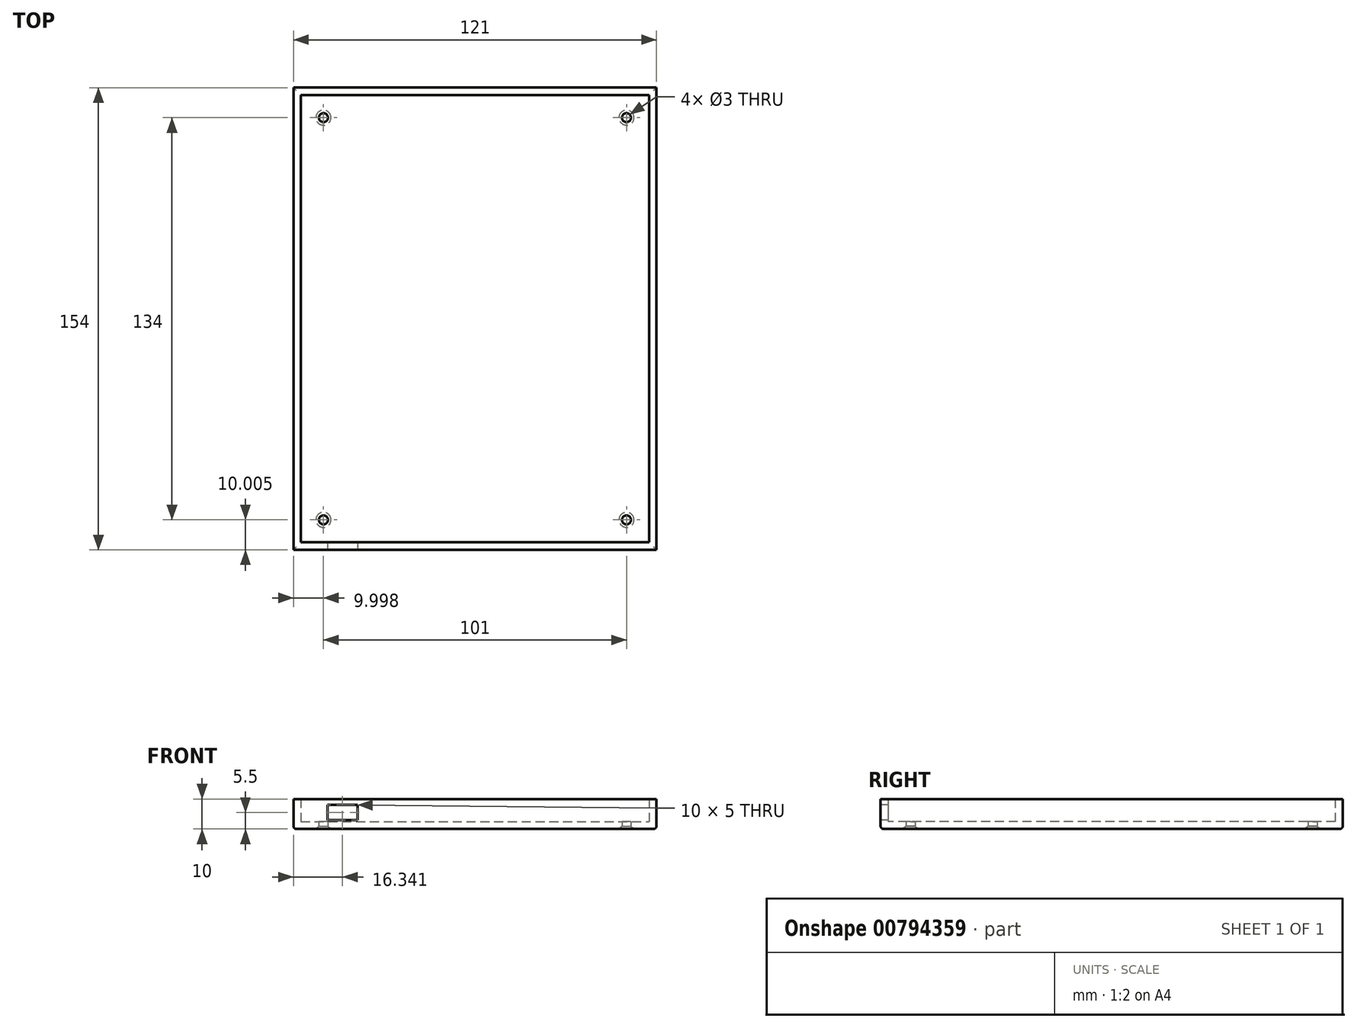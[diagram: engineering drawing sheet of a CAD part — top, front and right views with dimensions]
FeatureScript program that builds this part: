
annotation { "Feature Type Name" : "Feature", "Feature Type Description" : "" }
export const myFeature = defineFeature(function(context is Context, id is Id, definition is map)
    precondition{}
    {
        {
            var Q0;
            Q0=qCreatedBy(makeId("Top.planeOp"),FACE);
            var sketch = newSketch(context, id + "F0", { "sketchPlane" : qUnion([Q0])});
            skLineSegment(sketch, "E0.bottom", {"start": v(-90.74, 109.84) * mm, "end": v(30.26, 109.84) * mm});
            skLineSegment(sketch, "E0.top", {"start": v(-90.74, -44.16) * mm, "end": v(30.26, -44.16) * mm});
            skLineSegment(sketch, "E0.left", {"start": v(-90.74, 109.84) * mm, "end": v(-90.74, -44.16) * mm});
            skLineSegment(sketch, "E0.right", {"start": v(30.26, 109.84) * mm, "end": v(30.26, -44.16) * mm});
            skSolve(sketch);
        }
        {
            var Q0;
            Q0=makeQuery(id+"F0.imprint","IMPRINT",FACE,{"disambiguationData":[TD([[makeQuery(id+"F0.imprint","IMPRINT",EDGE,{"derivedFrom":sQuery(id+"F0.wireOp",EDGE,"E0.bottom")}),-1.0]])]});
            extrude(context, id + "F1", {"entities" : qUnion([Q0]), "depth" : 10 * mm, "offsetDistance" : 25 * mm});
        }
        {
            var Q0;
            Q0=makeQuery(id+"F1.opExtrude","CAP_FACE",FACE,{"disambiguationData":[OSD([sQuery(id+"F0.wireOp",EDGE,"E0.bottom"),sQuery(id+"F0.wireOp",EDGE,"E0.top"),sQuery(id+"F0.wireOp",EDGE,"E0.left"),sQuery(id+"F0.wireOp",EDGE,"E0.right")])],"isStart":false});
            shell(context, id + "F2", {"entities" : qUnion([Q0]), "thickness" : 2.5 * mm});
        }
        {
            var Q0;
            Q0=makeQuery(id+"F1.opExtrude","CAP_FACE",FACE,{"disambiguationData":[OSD([sQuery(id+"F0.wireOp",EDGE,"E0.bottom"),sQuery(id+"F0.wireOp",EDGE,"E0.top"),sQuery(id+"F0.wireOp",EDGE,"E0.left"),sQuery(id+"F0.wireOp",EDGE,"E0.right")])],"isStart":true});
            var sketch = newSketch(context, id + "F3", { "sketchPlane" : qUnion([Q0])});
            skPoint(sketch, "E1", {"position": v(-80.74, 34.16) * mm});
            skPoint(sketch, "E2", {"position": v(20.26, 34.16) * mm});
            skPoint(sketch, "E3", {"position": v(-80.74, -99.84) * mm});
            skPoint(sketch, "E4", {"position": v(20.26, -99.84) * mm});
            skSolve(sketch);
        }
        {
            var Q0;
            Q0=sQuery(id+"F3.wireOp",VERTEX,"E1");
            var Q1;
            Q1=sQuery(id+"F3.wireOp",VERTEX,"E2");
            var Q2;
            Q2=sQuery(id+"F3.wireOp",VERTEX,"E3");
            var Q3;
            Q3=sQuery(id+"F3.wireOp",VERTEX,"E4");
            var Q4;
            Q4=makeQuery(id+"F1.opExtrude","SWEPT_BODY",BODY,{"disambiguationData":[OSD([sQuery(id+"F0.wireOp",EDGE,"E0.bottom"),sQuery(id+"F0.wireOp",EDGE,"E0.top"),sQuery(id+"F0.wireOp",EDGE,"E0.left"),sQuery(id+"F0.wireOp",EDGE,"E0.right")])]});
            hole(context, id + "F4", {"style" : HoleStyle.C_SINK, "endStyle" : HoleEndStyle.THROUGH, "holeDiameter" : 3 * mm, "cSinkDiameter" : 5 * mm, "cSinkAngle" : 90 * degree, "majorDiameter" : 5 * mm, "isTappedThrough" : true, "tappedDepth" : 12 * mm, "tapClearance" : 3, "locations" : qUnion([Q0, Q1, Q2, Q3]), "scope" : qUnion([Q4])});
        }
        {
            var Q0;
            Q0=makeQuery(id+"F1.opExtrude","CAP_EDGE",EDGE,{"disambiguationData":[OSD([sQuery(id+"F0.wireOp",EDGE,"E0.top")])],"isStart":true});
            var Q1;
            Q1=makeQuery(id+"F1.opExtrude","CAP_EDGE",EDGE,{"disambiguationData":[OSD([sQuery(id+"F0.wireOp",EDGE,"E0.left")])],"isStart":true});
            var Q2;
            Q2=makeQuery(id+"F1.opExtrude","CAP_EDGE",EDGE,{"disambiguationData":[OSD([sQuery(id+"F0.wireOp",EDGE,"E0.right")])],"isStart":true});
            var Q3;
            Q3=makeQuery(id+"F1.opExtrude","CAP_EDGE",EDGE,{"disambiguationData":[OSD([sQuery(id+"F0.wireOp",EDGE,"E0.bottom")])],"isStart":true});
            fillet(context, id + "F5", {"entities" : qUnion([Q0, Q1, Q2, Q3]), "radius" : 1 * mm, "tangentPropagation" : true, "allowEdgeOverflow" : false});
        }
        {
            var Q0;
            Q0=makeQuery(id+"F1.opExtrude","SWEPT_FACE",FACE,{"disambiguationData":[OSD([sQuery(id+"F0.wireOp",EDGE,"E0.top")])]});
            var sketch = newSketch(context, id + "F6", { "sketchPlane" : qUnion([Q0])});
            skLineSegment(sketch, "E5.bottom", {"start": v(-69.4, 8) * mm, "end": v(-79.4, 8) * mm});
            skLineSegment(sketch, "E5.top", {"start": v(-69.4, 3) * mm, "end": v(-79.4, 3) * mm});
            skLineSegment(sketch, "E5.left", {"start": v(-69.4, 8) * mm, "end": v(-69.4, 3) * mm});
            skLineSegment(sketch, "E5.right", {"start": v(-79.4, 8) * mm, "end": v(-79.4, 3) * mm});
            skPoint(sketch, "E5.middle", {"position": v(-74.4, 5.5) * mm});
            skPoint(sketch, "E5.middle.positionSnap0", {"position": v(-90.74, 5.5) * mm});
            skPoint(sketch, "E5.centerSnap0", {"position": v(-90.74, 5.5) * mm});
            skSolve(sketch);
        }
        {
            var Q0;
            Q0 = qSketchRegion(id + "F6", true);
            var Q1;
            Q1=makeQuery(id+"F2.opShell","OFFSET_FACE",FACE,{"disambiguationData":[OSD([sQuery(id+"F0.wireOp",EDGE,"E0.top")])]});
            extrude(context, id + "F7", {"entities" : qUnion([Q0]), "operationType" : NewBodyOperationType.REMOVE, "endBound" : BoundingType.UP_TO_SURFACE, "oppositeDirection" : true, "depth" : 5 * mm, "endBoundEntityFace" : qUnion([Q1]), "offsetDistance" : 25 * mm});
        }
    });
